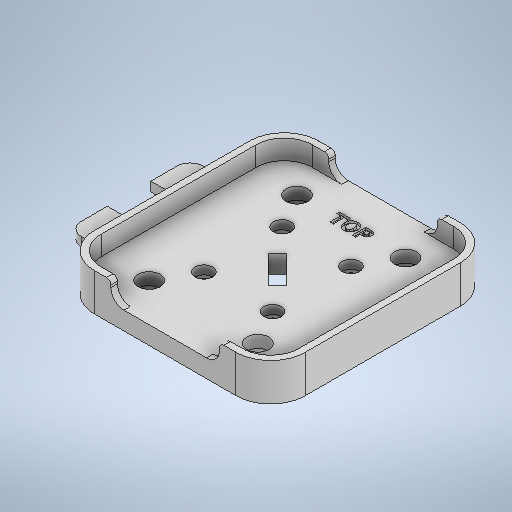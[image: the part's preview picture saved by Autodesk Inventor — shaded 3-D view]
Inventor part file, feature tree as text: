
AUTODESK INVENTOR PART (.ipt)
format: ipt  version: 2025 (Build 290162000, 162)  size: 456,192 bytes
history: native  units: mm
features: extrude x7, sketch x7, fillet x2, shell x1, thicken_offset x1, mirror x1, projected_geometry x1
ambient origin geometry x8: Origin, YZ Plane, XZ Plane, XY Plane, X Axis, Y Axis, Z Axis, Center Point
bodies: Solid1 (feature_tree)
feature tree (20):
  extrude  "Extrusion1"  Depth=51.6mm
  shell  "Shell1"  Thickness=8.0mm
  thicken_offset  "Thicken1"
  extrude  "Extrusion2"  Depth=1.5mm
  extrude  "Extrusion3"  Depth=9.0mm
  extrude  "Extrusion4"  Depth=3.0mm
  extrude  "Extrusion5"  Depth=24.3mm
  fillet  "Fillet1"  [1 undecoded]
  mirror  "Mirror1"
  extrude  "Extrusion6"  Depth=2.1mm
  fillet  "Fillet2"  Radius=18.0mm
  extrude  "Extrusion7"  Depth=25.0mm
  sketch  "Sketch1"  dims[d1=48.5mm d2=51.6mm d3=8.0mm]
  sketch  "Sketch2"  dims[d4=6.0mm d5=0.0mm d6=1.5mm]
  sketch  "Sketch3"  dims[d7=2.65mm d8=2.0mm d12=9.0mm]
  sketch  "Sketch4"  dims[d13=135.0deg d14=3.0mm]
  sketch  "Sketch5"  dims[d15=22.75mm d16=24.3mm d17=0.0mm d18=0.0mm]
  sketch  "Sketch6"  dims[d19=7.9mm d20=2.1mm d21=18.0mm]
  sketch  "Sketch7"  dims[d22=5.0mm d23=25.0mm d24=34.0mm d25=17.0mm d26=12.5mm d27=2.8mm d28=0.0mm d29=4.0mm d30=2.0mm d31=0.0mm d32=2.15mm d33=0.0mm d34=9.85mm d35=28.0mm d37=9.0mm d38=5.0mm d40=2.1mm d41=3.0mm d42=2.65mm d43=25.0mm d44=4.5mm d45=3.0mm d46=0.0mm d47=0.0mm d48=1.0mm d49=10.0mm d50=4.0mm d51=0.5mm d52=0.0mm]
  projected_geometry  "Project Cut Edges1"
note: 1 required parameter value undecoded (feature->parameter linkage not recoverable at this tier; creation-order binding heuristic only, values carry confidence <= 0.55)
